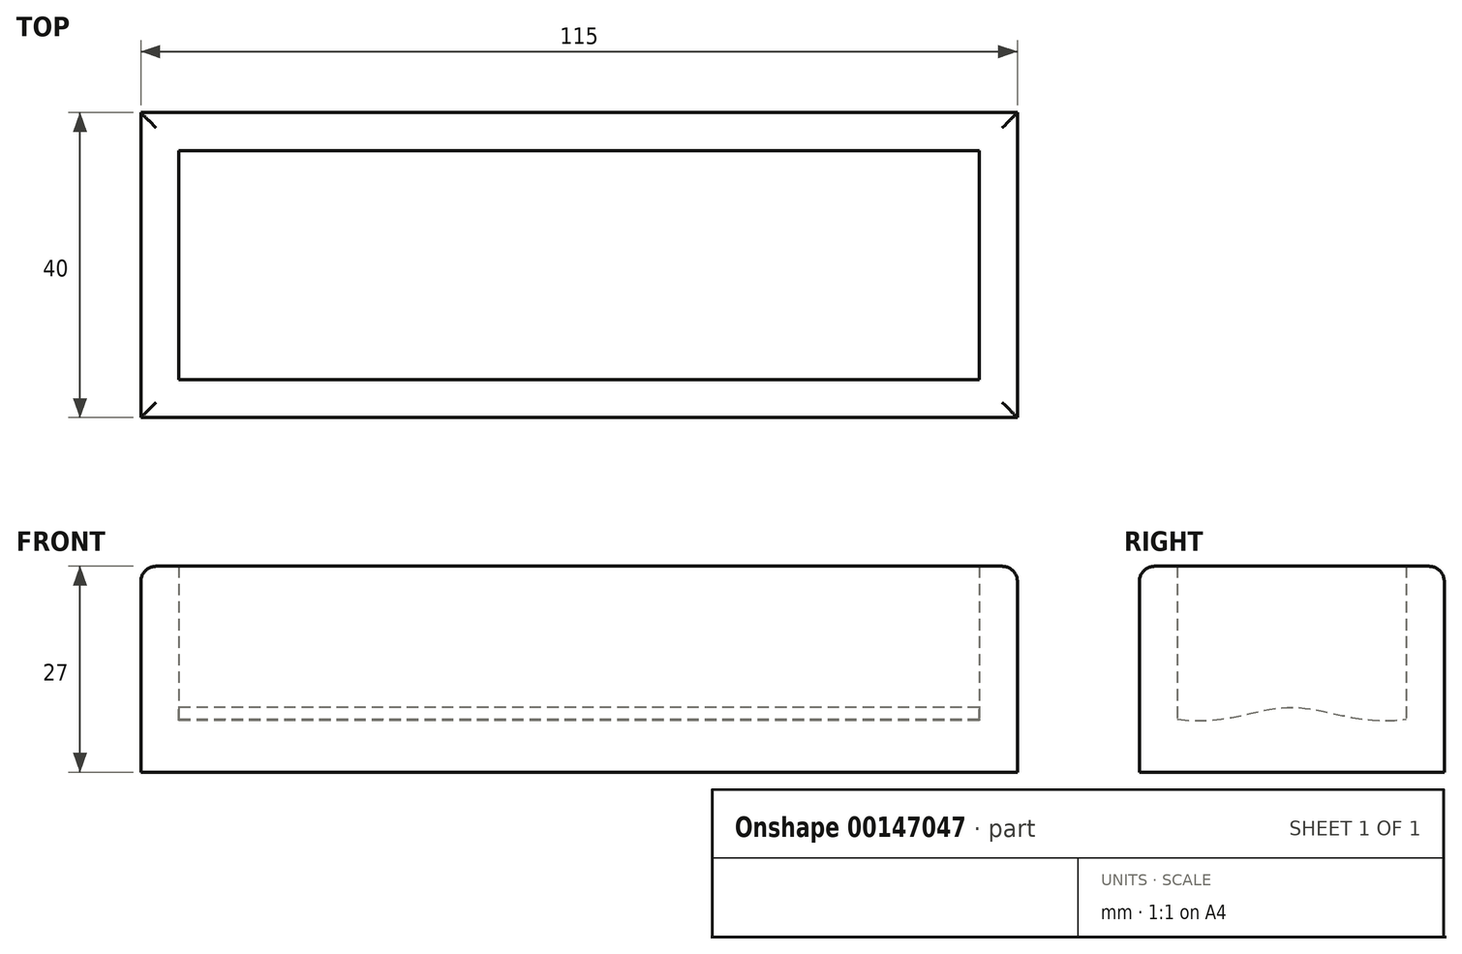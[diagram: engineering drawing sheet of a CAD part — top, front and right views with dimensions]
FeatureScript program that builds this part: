
annotation { "Feature Type Name" : "Feature", "Feature Type Description" : "" }
export const myFeature = defineFeature(function(context is Context, id is Id, definition is map)
    precondition{}
    {
        {
            var Q0;
            Q0=qCreatedBy(makeId("Top.planeOp"),FACE);
            var sketch = newSketch(context, id + "F0", { "sketchPlane" : qUnion([Q0])});
            skLineSegment(sketch, "E0.bottom", {"start": v(-52.5, 15) * mm, "end": v(52.5, 15) * mm});
            skLineSegment(sketch, "E0.top", {"start": v(-52.5, -15) * mm, "end": v(52.5, -15) * mm});
            skLineSegment(sketch, "E0.left", {"start": v(-52.5, 15) * mm, "end": v(-52.5, -15) * mm});
            skLineSegment(sketch, "E0.right", {"start": v(52.5, 15) * mm, "end": v(52.5, -15) * mm});
            skPoint(sketch, "E0.middle", {"position": v(0, 0) * mm});
            skLineSegment(sketch, "E1.bottom", {"start": v(-57.5, 20) * mm, "end": v(57.5, 20) * mm});
            skLineSegment(sketch, "E1.top", {"start": v(-57.5, -20) * mm, "end": v(57.5, -20) * mm});
            skLineSegment(sketch, "E1.left", {"start": v(-57.5, 20) * mm, "end": v(-57.5, -20) * mm});
            skLineSegment(sketch, "E1.right", {"start": v(57.5, 20) * mm, "end": v(57.5, -20) * mm});
            skSolve(sketch);
        }
        {
            var Q0;
            Q0=makeQuery(id+"F0.imprint","IMPRINT",FACE,{"disambiguationData":[TD([[makeQuery(id+"F0.imprint","IMPRINT",EDGE,{"derivedFrom":sQuery(id+"F0.wireOp",EDGE,"E0.bottom")}),-1.0]])]});
            var Q1;
            Q1=makeQuery(id+"F0.imprint","IMPRINT",FACE,{"disambiguationData":[TD([[makeQuery(id+"F0.imprint","IMPRINT",EDGE,{"derivedFrom":sQuery(id+"F0.wireOp",EDGE,"E0.bottom")}),1.0]])]});
            extrude(context, id + "F1", {"entities" : qUnion([Q0, Q1]), "oppositeDirection" : true, "depth" : 5 * mm});
        }
        {
            var Q0;
            Q0=makeQuery(id+"F0.imprint","IMPRINT",FACE,{"disambiguationData":[TD([[makeQuery(id+"F0.imprint","IMPRINT",EDGE,{"derivedFrom":sQuery(id+"F0.wireOp",EDGE,"E0.bottom")}),1.0]])]});
            extrude(context, id + "F2", {"entities" : qUnion([Q0]), "operationType" : NewBodyOperationType.ADD, "depth" : 22 * mm});
        }
        {
            var Q0;
            Q0=makeQuery(id+"F2.opExtrude","CAP_EDGE",EDGE,{"disambiguationData":[OSD([sQuery(id+"F0.wireOp",EDGE,"E1.bottom")])],"isStart":false});
            var Q1;
            Q1=makeQuery(id+"F2.opExtrude","CAP_EDGE",EDGE,{"disambiguationData":[OSD([sQuery(id+"F0.wireOp",EDGE,"E1.left")])],"isStart":false});
            var Q2;
            Q2=makeQuery(id+"F2.opExtrude","CAP_EDGE",EDGE,{"disambiguationData":[OSD([sQuery(id+"F0.wireOp",EDGE,"E1.top")])],"isStart":false});
            var Q3;
            Q3=makeQuery(id+"F2.opExtrude","CAP_EDGE",EDGE,{"disambiguationData":[OSD([sQuery(id+"F0.wireOp",EDGE,"E1.right")])],"isStart":false});
            fillet(context, id + "F3", {"entities" : qUnion([Q0, Q1, Q2, Q3]), "radius" : 2 * mm, "tangentPropagation" : true, "allowEdgeOverflow" : false});
        }
        {
            var Q0;
            Q0=makeQuery(id+"F2.opExtrude","SWEPT_FACE",FACE,{"disambiguationData":[OSD([sQuery(id+"F0.wireOp",EDGE,"E0.right")])]});
            var sketch = newSketch(context, id + "F4", { "sketchPlane" : qUnion([Q0])});
            skLineSegment(sketch, "E2", {"start": v(-15, 0) * mm, "end": v(-15, 1.96) * mm});
            skLineSegment(sketch, "E3", {"start": v(-15, 0) * mm, "end": v(15, 0) * mm});
            skLineSegment(sketch, "E4", {"start": v(15, 0) * mm, "end": v(15, 1.96) * mm});
            skFitSpline(sketch, "E5", {"points": [v(15, 1.96) * mm, v(0, 3.5) * mm, v(-15, 1.96) * mm], "startDerivative": vector(-36, -5.79) * mm, "endDerivative": vector(-36, 5.79) * mm});
            skSolve(sketch);
        }
        {
            var Q0;
            Q0=makeQuery(id+"F4.imprint","IMPRINT",FACE,{"disambiguationData":[TD([[makeQuery(id+"F4.imprint","IMPRINT",EDGE,{"derivedFrom":sQuery(id+"F4.wireOp",EDGE,"E2")}),1.0]])]});
            extrude(context, id + "F5", {"entities" : qUnion([Q0]), "operationType" : NewBodyOperationType.ADD, "endBound" : BoundingType.UP_TO_NEXT, "depth" : 25 * mm});
        }
    });
